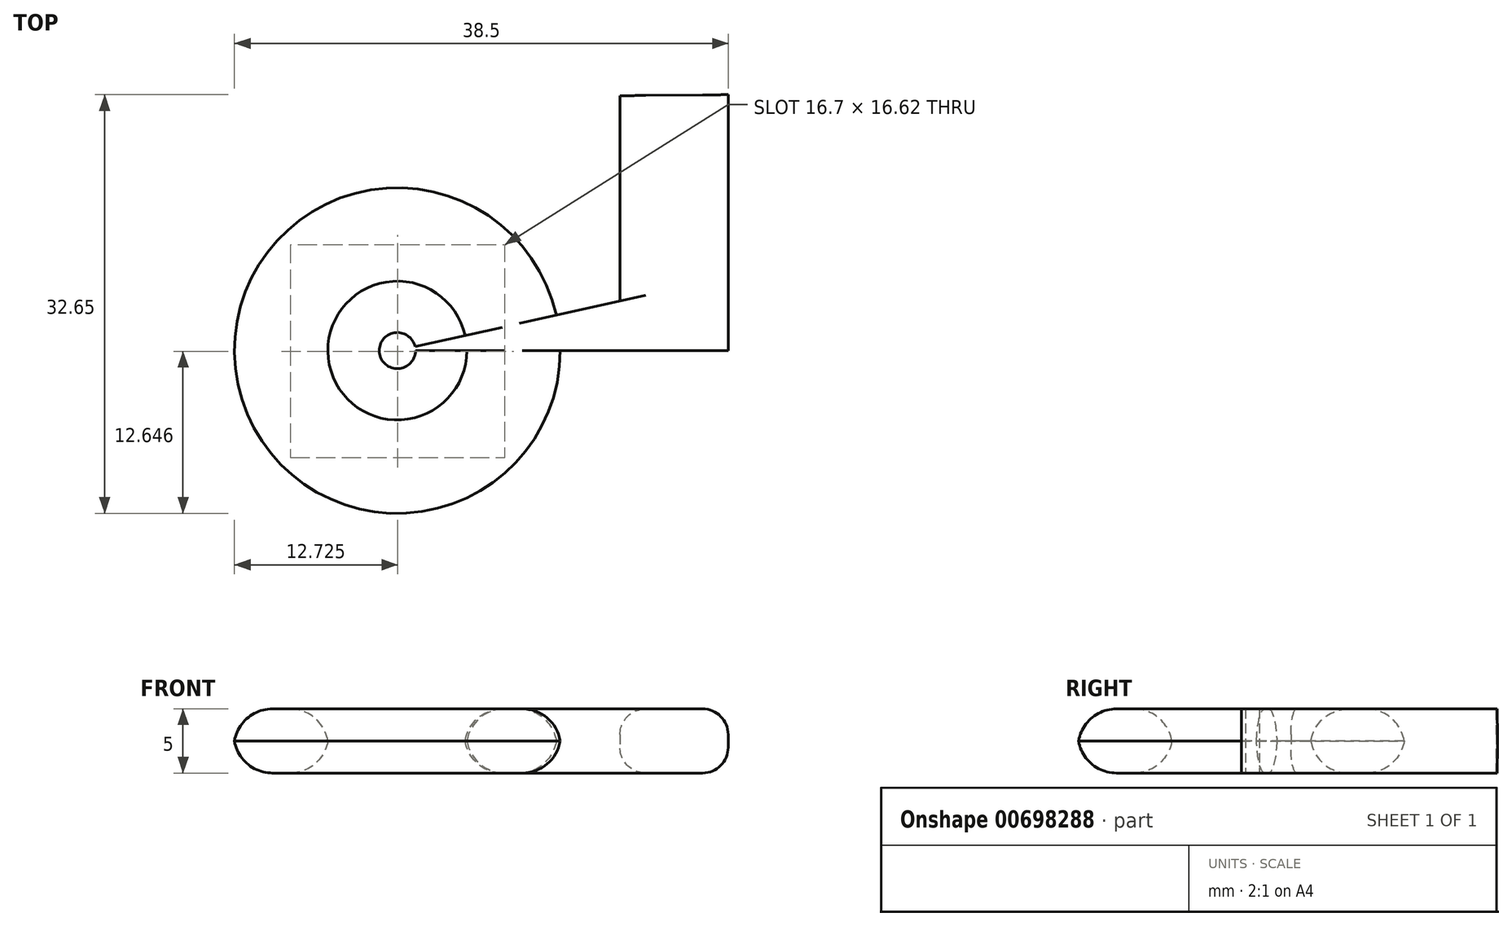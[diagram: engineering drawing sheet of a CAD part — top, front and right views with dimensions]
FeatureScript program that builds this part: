
annotation { "Feature Type Name" : "Feature", "Feature Type Description" : "" }
export const myFeature = defineFeature(function(context is Context, id is Id, definition is map)
    precondition{}
    {
        {
            var Q0;
            Q0=qCreatedBy(makeId("Top.planeOp"),FACE);
            var sketch = newSketch(context, id + "F0", { "sketchPlane" : qUnion([Q0])});
            skCircle(sketch, "E0", {"center": v(-20.86, -14.31) * mm, "radius": 12.74 * mm});
            skCircle(sketch, "E1", {"center": v(-20.86, -14.31) * mm, "radius": 5.37 * mm});
            skLineSegment(sketch, "E2", {"start": v(-20.86, -14.31) * mm, "end": v(-3.5, -10.45) * mm});
            skLineSegment(sketch, "E3", {"start": v(-20.86, -14.31) * mm, "end": v(4.94, -14.31) * mm});
            skLineSegment(sketch, "E4", {"start": v(4.94, -14.31) * mm, "end": v(4.94, 5.64) * mm});
            skLineSegment(sketch, "E5", {"start": v(-3.5, -10.45) * mm, "end": v(-3.5, 5.56) * mm});
            skLineSegment(sketch, "E6", {"start": v(-3.5, 5.56) * mm, "end": v(4.94, 5.64) * mm});
            skLineSegment(sketch, "E7", {"start": v(-3.5, -10.45) * mm, "end": v(4.94, -14.31) * mm});
            skCircle(sketch, "E8", {"center": v(-20.86, -14.31) * mm, "radius": 1.41 * mm});
            skSolve(sketch);
        }
        {
            var Q0;
            {var subQ0=sQuery(id+"F0.wireOp",EDGE,"E2");var subQ1=sQuery(id+"F0.wireOp",EDGE,"E0");var subQ2=makeQuery(id+"F0.imprint","INTERSECT",VERTEX,{"derivedFrom":[subQ1,subQ0]});Q0=makeQuery(id+"F0.imprint","IMPRINT",FACE,{"disambiguationData":[TD([[makeQuery(id+"F0.imprint","IMPRINT",EDGE,{"disambiguationData":[TD([[subQ2,-1.0]])],"derivedFrom":subQ1}),1.0]])]});}
            var Q1;
            {var subQ0=sQuery(id+"F0.wireOp",EDGE,"E2");var subQ1=sQuery(id+"F0.wireOp",EDGE,"E1");var subQ2=makeQuery(id+"F0.imprint","INTERSECT",VERTEX,{"derivedFrom":[subQ1,subQ0]});Q1=makeQuery(id+"F0.imprint","IMPRINT",FACE,{"disambiguationData":[TD([[makeQuery(id+"F0.imprint","IMPRINT",EDGE,{"disambiguationData":[TD([[subQ2,1.0]])],"derivedFrom":subQ1}),1.0]])]});}
            var Q2;
            {var subQ0=sQuery(id+"F0.wireOp",EDGE,"E2");var subQ1=sQuery(id+"F0.wireOp",EDGE,"E0");var subQ2=makeQuery(id+"F0.imprint","INTERSECT",VERTEX,{"derivedFrom":[subQ1,subQ0]});Q2=makeQuery(id+"F0.imprint","IMPRINT",FACE,{"disambiguationData":[TD([[makeQuery(id+"F0.imprint","IMPRINT",EDGE,{"disambiguationData":[TD([[subQ2,1.0]])],"derivedFrom":subQ1}),1.0]])]});}
            var Q3;
            {var subQ5=sQuery(id+"F0.wireOp",EDGE,"E7");Q3=makeQuery(id+"F0.imprint","IMPRINT",FACE,{"disambiguationData":[TD([[makeQuery(id+"F0.imprint","IMPRINT",EDGE,{"derivedFrom":subQ5}),-1.0]])]});}
            var Q4;
            {var subQ0=sQuery(id+"F0.wireOp",EDGE,"E3");var subQ1=sQuery(id+"F0.wireOp",EDGE,"E2");var subQ2=makeQuery(id+"F0.imprint","INTERSECT",VERTEX,{"derivedFrom":[subQ1,subQ0]});Q4=makeQuery(id+"F0.imprint","IMPRINT",FACE,{"disambiguationData":[TD([[makeQuery(id+"F0.imprint","IMPRINT",EDGE,{"disambiguationData":[TD([[subQ2,-1.0]])],"derivedFrom":subQ1}),1.0]])]});}
            var Q5;
            {var subQ0=sQuery(id+"F0.wireOp",EDGE,"E3");var subQ1=sQuery(id+"F0.wireOp",EDGE,"E2");var subQ2=makeQuery(id+"F0.imprint","INTERSECT",VERTEX,{"derivedFrom":[subQ1,subQ0]});Q5=makeQuery(id+"F0.imprint","IMPRINT",FACE,{"disambiguationData":[TD([[makeQuery(id+"F0.imprint","IMPRINT",EDGE,{"disambiguationData":[TD([[subQ2,-1.0]])],"derivedFrom":subQ1}),-1.0]])]});}
            var Q6;
            {var subQ0=sQuery(id+"F0.wireOp",EDGE,"E3");var subQ1=sQuery(id+"F0.wireOp",EDGE,"E0");var subQ2=makeQuery(id+"F0.imprint","INTERSECT",VERTEX,{"derivedFrom":[subQ1,subQ0]});Q6=makeQuery(id+"F0.imprint","IMPRINT",FACE,{"disambiguationData":[TD([[makeQuery(id+"F0.imprint","IMPRINT",EDGE,{"disambiguationData":[TD([[subQ2,1.0]])],"derivedFrom":subQ1}),1.0]])]});}
            var Q7;
            {var subQ5=sQuery(id+"F0.wireOp",EDGE,"E3");var subQ7=sQuery(id+"F0.wireOp",EDGE,"E0");var subQ8=makeQuery(id+"F0.imprint","INTERSECT",VERTEX,{"derivedFrom":[subQ7,subQ5]});Q7=makeQuery(id+"F0.imprint","IMPRINT",FACE,{"disambiguationData":[TD([[makeQuery(id+"F0.imprint","IMPRINT",EDGE,{"disambiguationData":[TD([[subQ8,-1.0]])],"derivedFrom":subQ7}),1.0]])]});}
            var Q8;
            Q8=makeQuery(id+"F0.imprint","IMPRINT",FACE,{"disambiguationData":[TD([[makeQuery(id+"F0.imprint","IMPRINT",EDGE,{"derivedFrom":sQuery(id+"F0.wireOp",EDGE,"E4")}),1.0]])]});
            extrude(context, id + "F1", {"entities" : qUnion([Q0, Q1, Q2, Q3, Q4, Q5, Q6, Q7, Q8]), "endBound" : BoundingType.SYMMETRIC, "depth" : 5 * mm, "offsetDistance" : 25.4 * mm});
        }
        {
            var Q0;
            Q0=makeQuery(id+"F1.opExtrude","CAP_EDGE",EDGE,{"disambiguationData":[OSD([sQuery(id+"F0.wireOp",EDGE,"E5")])],"isStart":false});
            var Q1;
            Q1=makeQuery(id+"F1.opExtrude","CAP_EDGE",EDGE,{"disambiguationData":[OSD([sQuery(id+"F0.wireOp",EDGE,"E4")])],"isStart":false});
            var Q2;
            Q2=makeQuery(id+"F1.opExtrude","CAP_EDGE",EDGE,{"disambiguationData":[OSD([sQuery(id+"F0.wireOp",EDGE,"E4")])],"isStart":true});
            var Q3;
            Q3=makeQuery(id+"F1.opExtrude","CAP_EDGE",EDGE,{"disambiguationData":[OSD([sQuery(id+"F0.wireOp",EDGE,"E5")])],"isStart":true});
            fillet(context, id + "F2", {"entities" : qUnion([Q0, Q1, Q2, Q3]), "radius" : 2 * mm, "tangentPropagation" : true, "allowEdgeOverflow" : false});
        }
        {
            var Q0;
            Q0=makeQuery(id+"F1.opExtrude","CAP_EDGE",EDGE,{"disambiguationData":[OSD([sQuery(id+"F0.wireOp",EDGE,"E0")])],"isStart":false});
            var Q1;
            Q1=makeQuery(id+"F1.opExtrude","CAP_EDGE",EDGE,{"disambiguationData":[OSD([sQuery(id+"F0.wireOp",EDGE,"E1")])],"isStart":false});
            var Q2;
            Q2=makeQuery(id+"F1.opExtrude","CAP_EDGE",EDGE,{"disambiguationData":[OSD([sQuery(id+"F0.wireOp",EDGE,"E0")])],"isStart":true});
            var Q3;
            Q3=makeQuery(id+"F1.opExtrude","CAP_EDGE",EDGE,{"disambiguationData":[OSD([sQuery(id+"F0.wireOp",EDGE,"E1")])],"isStart":true});
            fillet(context, id + "F3", {"entities" : qUnion([Q0, Q1, Q2, Q3]), "radius" : 3 * mm, "tangentPropagation" : true, "allowEdgeOverflow" : false});
        }
    });
